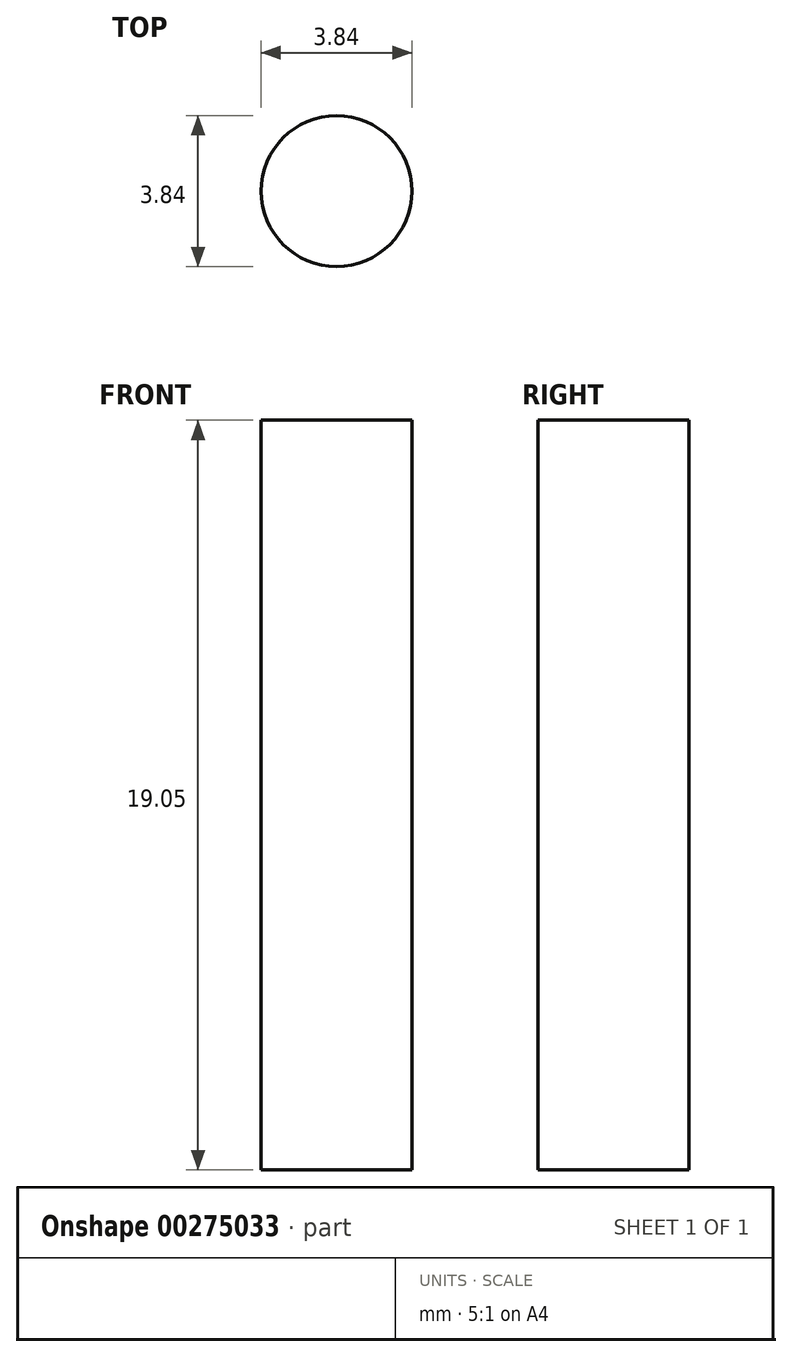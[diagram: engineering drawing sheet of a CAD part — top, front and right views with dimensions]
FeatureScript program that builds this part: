
annotation { "Feature Type Name" : "Feature", "Feature Type Description" : "" }
export const myFeature = defineFeature(function(context is Context, id is Id, definition is map)
    precondition{}
    {
        {
            var Q0;
            Q0=qCreatedBy(makeId("Top.planeOp"),FACE);
            var sketch = newSketch(context, id + "F0", { "sketchPlane" : qUnion([Q0])});
            skCircle(sketch, "E0", {"center": v(0, 0) * mm, "radius": 1.92 * mm});
            skSolve(sketch);
        }
        {
            var Q0;
            Q0 = qSketchRegion(id + "F0", true);
            extrude(context, id + "F1", {"entities" : qUnion([Q0]), "depth" : 19.05 * mm});
        }
    });
